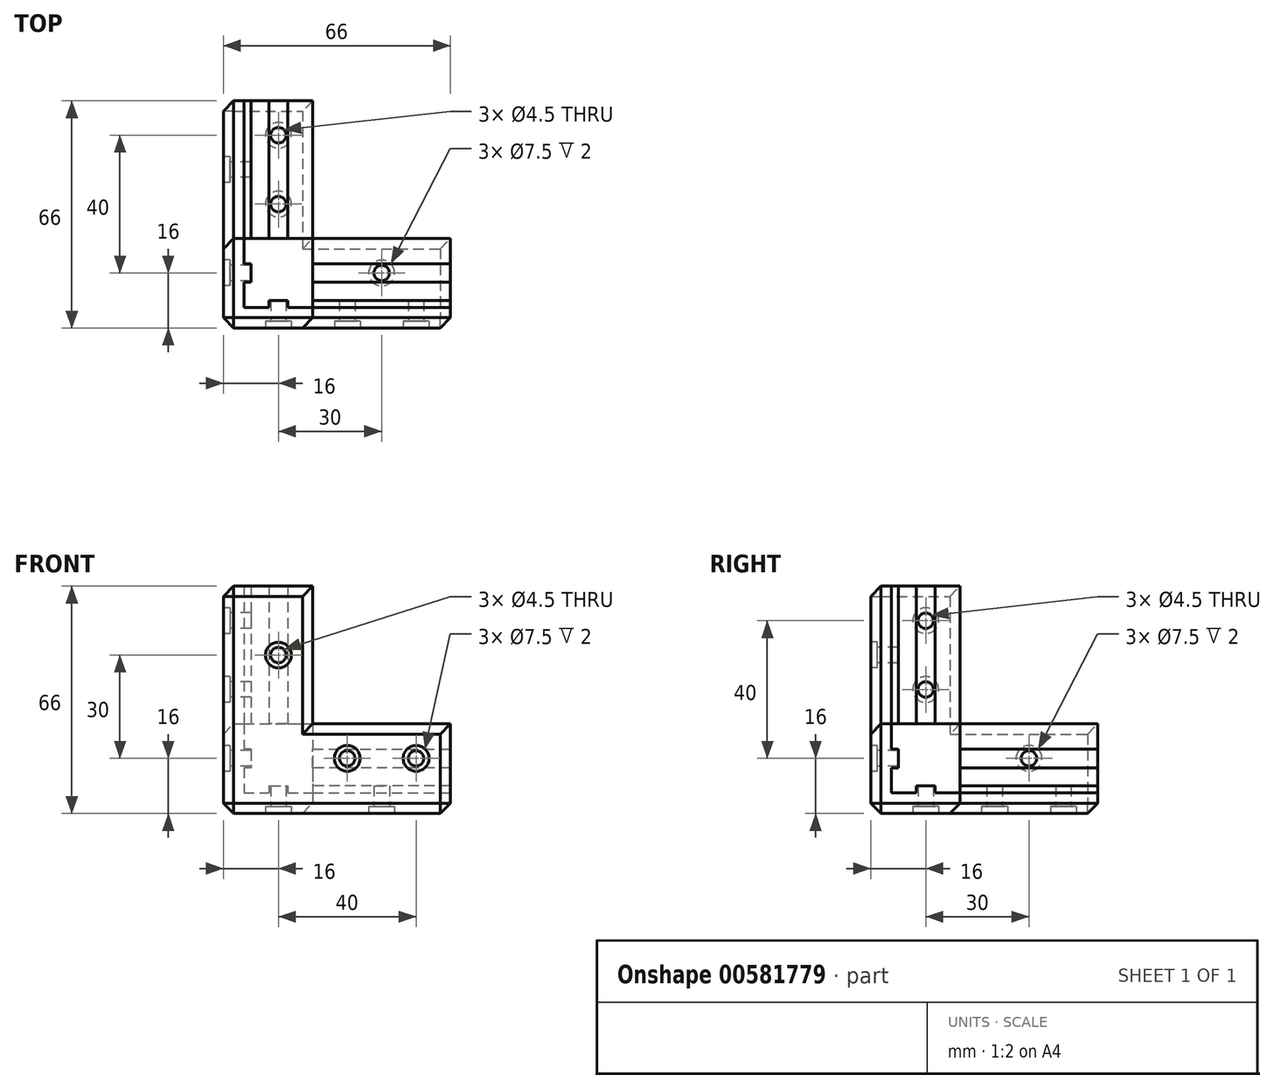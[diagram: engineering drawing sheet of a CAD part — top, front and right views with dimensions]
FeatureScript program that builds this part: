
annotation { "Feature Type Name" : "Feature", "Feature Type Description" : "" }
export const myFeature = defineFeature(function(context is Context, id is Id, definition is map)
    precondition{}
    {
        {
            var Q0;
            Q0=qCreatedBy(makeId("Top.planeOp"),FACE);
            var sketch = newSketch(context, id + "F0", { "sketchPlane" : qUnion([Q0])});
            skLineSegment(sketch, "E0", {"start": v(0, 0) * mm, "end": v(0, 66) * mm});
            skLineSegment(sketch, "E1", {"start": v(0, 66) * mm, "end": v(26, 66) * mm});
            skLineSegment(sketch, "E2", {"start": v(26, 66) * mm, "end": v(26, 26) * mm});
            skLineSegment(sketch, "E3", {"start": v(26, 26) * mm, "end": v(66, 26) * mm});
            skLineSegment(sketch, "E4", {"start": v(66, 26) * mm, "end": v(66, 0) * mm});
            skLineSegment(sketch, "E5", {"start": v(66, 0) * mm, "end": v(0, 0) * mm});
            skLineSegment(sketch, "E6", {"start": v(66, 6) * mm, "end": v(6, 6) * mm, "construction": true});
            skLineSegment(sketch, "E7", {"start": v(6, 6) * mm, "end": v(6, 66) * mm, "construction": true});
            skSolve(sketch);
        }
        {
            var Q0;
            Q0=qSketchRegion(id+"F0",true);
            extrude(context, id + "F1", {"entities" : qUnion([Q0]), "depth" : 6 * mm});
        }
        {
            var Q0;
            Q0=makeQuery(id+"F1.opExtrude","CAP_FACE",FACE,{"disambiguationData":[OSD([sQuery(id+"F0.wireOp",EDGE,"E0"),sQuery(id+"F0.wireOp",EDGE,"E1"),sQuery(id+"F0.wireOp",EDGE,"E2"),sQuery(id+"F0.wireOp",EDGE,"E3"),sQuery(id+"F0.wireOp",EDGE,"E4"),sQuery(id+"F0.wireOp",EDGE,"E5")])],"isStart":false});
            var sketch = newSketch(context, id + "F2", { "sketchPlane" : qUnion([Q0])});
            skLineSegment(sketch, "E8", {"start": v(0, 66) * mm, "end": v(6, 66) * mm});
            skLineSegment(sketch, "E9", {"start": v(6, 66) * mm, "end": v(6, 6) * mm});
            skLineSegment(sketch, "E10", {"start": v(6, 6) * mm, "end": v(66, 6) * mm});
            skLineSegment(sketch, "E11", {"start": v(66, 6) * mm, "end": v(66, 0) * mm});
            skLineSegment(sketch, "E12", {"start": v(66, 0) * mm, "end": v(0, 0) * mm});
            skLineSegment(sketch, "E13", {"start": v(0, 0) * mm, "end": v(0, 66) * mm});
            skSolve(sketch);
        }
        {
            var Q0;
            Q0=makeQuery(id+"F2.imprint","IMPRINT",FACE,{"disambiguationData":[TD([[makeQuery(id+"F2.imprint","IMPRINT",EDGE,{"derivedFrom":sQuery(id+"F2.wireOp",EDGE,"E8")}),-1.0]])]});
            extrude(context, id + "F3", {"entities" : qUnion([Q0]), "operationType" : NewBodyOperationType.ADD, "depth" : 20 * mm});
        }
        {
            var Q0;
            Q0=makeQuery(id+"F3.opExtrude","CAP_FACE",FACE,{"disambiguationData":[OSD([sQuery(id+"F2.wireOp",EDGE,"E8"),sQuery(id+"F2.wireOp",EDGE,"E9"),sQuery(id+"F2.wireOp",EDGE,"E10"),sQuery(id+"F2.wireOp",EDGE,"E11"),sQuery(id+"F2.wireOp",EDGE,"E12"),sQuery(id+"F2.wireOp",EDGE,"E13")])],"isStart":false});
            var sketch = newSketch(context, id + "F4", { "sketchPlane" : qUnion([Q0])});
            skLineSegment(sketch, "E14", {"start": v(6, 26) * mm, "end": v(0, 26) * mm});
            skLineSegment(sketch, "E15", {"start": v(0, 26) * mm, "end": v(0, 0) * mm});
            skLineSegment(sketch, "E16", {"start": v(0, 0) * mm, "end": v(26, 0) * mm});
            skLineSegment(sketch, "E17", {"start": v(26, 0) * mm, "end": v(26, 6) * mm});
            skLineSegment(sketch, "E18", {"start": v(26, 6) * mm, "end": v(6, 6) * mm});
            skLineSegment(sketch, "E19", {"start": v(6, 6) * mm, "end": v(6, 26) * mm});
            skSolve(sketch);
        }
        {
            var Q0;
            Q0=qSketchRegion(id+"F4",true);
            extrude(context, id + "F5", {"entities" : qUnion([Q0]), "operationType" : NewBodyOperationType.ADD, "depth" : 40 * mm});
        }
        {
            var Q0;
            Q0=makeQuery(id+"F1.opExtrude","CAP_FACE",FACE,{"disambiguationData":[OSD([sQuery(id+"F0.wireOp",EDGE,"E0"),sQuery(id+"F0.wireOp",EDGE,"E1"),sQuery(id+"F0.wireOp",EDGE,"E2"),sQuery(id+"F0.wireOp",EDGE,"E3"),sQuery(id+"F0.wireOp",EDGE,"E4"),sQuery(id+"F0.wireOp",EDGE,"E5")])],"isStart":false});
            var sketch = newSketch(context, id + "F6", { "sketchPlane" : qUnion([Q0])});
            skLineSegment(sketch, "E20", {"start": v(66, 16) * mm, "end": v(6, 16) * mm, "construction": true});
            skLineSegment(sketch, "E21", {"start": v(16, 66) * mm, "end": v(16, 6) * mm, "construction": true});
            skLineSegment(sketch, "E22", {"start": v(16, 6) * mm, "end": v(18.71, 6) * mm});
            skLineSegment(sketch, "E23", {"start": v(18.71, 6) * mm, "end": v(18.71, 8) * mm});
            skLineSegment(sketch, "E24", {"start": v(18.71, 8) * mm, "end": v(13.3, 8) * mm});
            skLineSegment(sketch, "E25", {"start": v(13.3, 8) * mm, "end": v(13.3, 6) * mm});
            skLineSegment(sketch, "E26", {"start": v(13.3, 6) * mm, "end": v(16, 6) * mm});
            skLineSegment(sketch, "E27", {"start": v(6, 16) * mm, "end": v(6, 18.7) * mm});
            skLineSegment(sketch, "E28", {"start": v(6, 18.7) * mm, "end": v(8, 18.7) * mm});
            skLineSegment(sketch, "E29", {"start": v(8, 18.7) * mm, "end": v(8, 13.29) * mm});
            skLineSegment(sketch, "E30", {"start": v(8, 13.29) * mm, "end": v(6, 13.29) * mm});
            skLineSegment(sketch, "E31", {"start": v(6, 13.29) * mm, "end": v(6, 16) * mm});
            skSolve(sketch);
        }
        {
            var Q0;
            Q0=qSketchRegion(id+"F6",true);
            extrude(context, id + "F7", {"entities" : qUnion([Q0]), "operationType" : NewBodyOperationType.ADD, "depth" : 60 * mm});
        }
        {
            var Q0;
            Q0=makeQuery(id+"F1.opExtrude","CAP_FACE",FACE,{"disambiguationData":[OSD([sQuery(id+"F0.wireOp",EDGE,"E0"),sQuery(id+"F0.wireOp",EDGE,"E1"),sQuery(id+"F0.wireOp",EDGE,"E2"),sQuery(id+"F0.wireOp",EDGE,"E3"),sQuery(id+"F0.wireOp",EDGE,"E4"),sQuery(id+"F0.wireOp",EDGE,"E5")])],"isStart":false});
            var sketch = newSketch(context, id + "F8", { "sketchPlane" : qUnion([Q0])});
            skLineSegment(sketch, "E32", {"start": v(66, 16) * mm, "end": v(8, 16) * mm, "construction": true});
            skLineSegment(sketch, "E33", {"start": v(66, 16) * mm, "end": v(66, 18.7) * mm});
            skLineSegment(sketch, "E34", {"start": v(66, 18.7) * mm, "end": v(26, 18.7) * mm});
            skLineSegment(sketch, "E35", {"start": v(26, 18.7) * mm, "end": v(26, 13.29) * mm});
            skLineSegment(sketch, "E36", {"start": v(26, 13.29) * mm, "end": v(66, 13.29) * mm});
            skLineSegment(sketch, "E37", {"start": v(66, 13.29) * mm, "end": v(66, 16) * mm});
            skLineSegment(sketch, "E38", {"start": v(16, 66) * mm, "end": v(16, 8) * mm, "construction": true});
            skLineSegment(sketch, "E39", {"start": v(16, 66) * mm, "end": v(13.3, 66) * mm});
            skLineSegment(sketch, "E40", {"start": v(13.3, 66) * mm, "end": v(13.3, 26) * mm});
            skLineSegment(sketch, "E41", {"start": v(13.3, 26) * mm, "end": v(18.7, 26) * mm});
            skLineSegment(sketch, "E42", {"start": v(18.7, 26) * mm, "end": v(18.7, 66) * mm});
            skLineSegment(sketch, "E43", {"start": v(18.7, 66) * mm, "end": v(16, 66) * mm});
            skSolve(sketch);
        }
        {
            var Q0;
            Q0=qSketchRegion(id+"F8",true);
            extrude(context, id + "F9", {"entities" : qUnion([Q0]), "operationType" : NewBodyOperationType.ADD, "depth" : 2 * mm});
        }
        {
            var Q0;
            {var subQ1=sQuery(id+"F2.wireOp",EDGE,"E10");var subQ2=sQuery(id+"F0.wireOp",EDGE,"E4");var subQ3=sQuery(id+"F4.wireOp",EDGE,"E18");Q0=makeQuery(id+"F7.boolean.opBoolean","SPLIT",FACE,{"disambiguationData":[TD([makeQuery(id+"F1.opExtrude","SWEPT_FACE",FACE,{"disambiguationData":[OSD([subQ2])]})])],"derivedFrom":makeQuery(id+"F5.boolean.opBoolean","MERGE",FACE,{"derivedFrom":[makeQuery(id+"F3.opExtrude","SWEPT_FACE",FACE,{"disambiguationData":[OSD([subQ1])]}),makeQuery(id+"F5.opExtrude","SWEPT_FACE",FACE,{"disambiguationData":[OSD([subQ3])]})]})});}
            var sketch = newSketch(context, id + "F10", { "sketchPlane" : qUnion([Q0])});
            skLineSegment(sketch, "E44", {"start": v(-66, 16) * mm, "end": v(-26, 16) * mm, "construction": true});
            skLineSegment(sketch, "E45", {"start": v(-66, 16) * mm, "end": v(-66, 13.3) * mm});
            skLineSegment(sketch, "E46", {"start": v(-66, 13.3) * mm, "end": v(-26, 13.3) * mm});
            skLineSegment(sketch, "E47", {"start": v(-26, 13.3) * mm, "end": v(-26, 16) * mm});
            skLineSegment(sketch, "E48", {"start": v(-26, 18.71) * mm, "end": v(-66, 18.71) * mm});
            skLineSegment(sketch, "E49", {"start": v(-66, 18.71) * mm, "end": v(-66, 16) * mm});
            skLineSegment(sketch, "E50", {"start": v(-26, 18.71) * mm, "end": v(-26, 16) * mm});
            skSolve(sketch);
        }
        {
            var Q0;
            Q0=qSketchRegion(id+"F10",true);
            extrude(context, id + "F11", {"entities" : qUnion([Q0]), "operationType" : NewBodyOperationType.ADD, "depth" : 2 * mm});
        }
        {
            var Q0;
            {var subQ0=sQuery(id+"F2.wireOp",EDGE,"E9");var subQ3=sQuery(id+"F0.wireOp",EDGE,"E1");var subQ5=sQuery(id+"F4.wireOp",EDGE,"E19");Q0=makeQuery(id+"F7.boolean.opBoolean","SPLIT",FACE,{"disambiguationData":[TD([makeQuery(id+"F1.opExtrude","SWEPT_FACE",FACE,{"disambiguationData":[OSD([subQ3])]})])],"derivedFrom":makeQuery(id+"F5.boolean.opBoolean","MERGE",FACE,{"derivedFrom":[makeQuery(id+"F3.opExtrude","SWEPT_FACE",FACE,{"disambiguationData":[OSD([subQ0])]}),makeQuery(id+"F5.opExtrude","SWEPT_FACE",FACE,{"disambiguationData":[OSD([subQ5])]})]})});}
            var sketch = newSketch(context, id + "F12", { "sketchPlane" : qUnion([Q0])});
            skLineSegment(sketch, "E51", {"start": v(66, 16) * mm, "end": v(26, 16) * mm, "construction": true});
            skLineSegment(sketch, "E52", {"start": v(66, 16) * mm, "end": v(66, 18.71) * mm});
            skLineSegment(sketch, "E53", {"start": v(66, 18.71) * mm, "end": v(26, 18.7) * mm});
            skLineSegment(sketch, "E54", {"start": v(26, 18.7) * mm, "end": v(26, 13.29) * mm});
            skLineSegment(sketch, "E55", {"start": v(26, 13.29) * mm, "end": v(66, 13.29) * mm});
            skLineSegment(sketch, "E56", {"start": v(66, 16) * mm, "end": v(66, 13.29) * mm});
            skSolve(sketch);
        }
        {
            var Q0;
            Q0=qSketchRegion(id+"F12",true);
            extrude(context, id + "F13", {"entities" : qUnion([Q0]), "operationType" : NewBodyOperationType.ADD, "depth" : 2 * mm});
        }
        {
            var Q0;
            Q0=makeQuery(id+"F5.boolean.opBoolean","MERGE",FACE,{"derivedFrom":[makeQuery(id+"F3.boolean.opBoolean","MERGE",FACE,{"derivedFrom":[makeQuery(id+"F1.opExtrude","SWEPT_FACE",FACE,{"disambiguationData":[OSD([sQuery(id+"F0.wireOp",EDGE,"E5")])]}),makeQuery(id+"F3.opExtrude","SWEPT_FACE",FACE,{"disambiguationData":[OSD([sQuery(id+"F2.wireOp",EDGE,"E12")])]})]}),makeQuery(id+"F5.opExtrude","SWEPT_FACE",FACE,{"disambiguationData":[OSD([sQuery(id+"F4.wireOp",EDGE,"E16")])]})]});
            var sketch = newSketch(context, id + "F14", { "sketchPlane" : qUnion([Q0])});
            skLineSegment(sketch, "E57", {"start": v(6, 66) * mm, "end": v(6, 6) * mm, "construction": true});
            skLineSegment(sketch, "E58", {"start": v(6, 6) * mm, "end": v(66, 6) * mm, "construction": true});
            skCircle(sketch, "E59", {"center": v(56, 16) * mm, "radius": 2.25 * mm});
            skCircle(sketch, "E60", {"center": v(36, 16) * mm, "radius": 2.25 * mm});
            skCircle(sketch, "E61", {"center": v(16, 46) * mm, "radius": 2.25 * mm});
            skLineSegment(sketch, "E62", {"start": v(26, 26) * mm, "end": v(6, 26) * mm, "construction": true});
            skLineSegment(sketch, "E63", {"start": v(26, 26) * mm, "end": v(26, 6) * mm, "construction": true});
            skSolve(sketch);
        }
        {
            var Q0;
            Q0=makeQuery(id+"F14.imprint","IMPRINT",FACE,{"disambiguationData":[TD([[makeQuery(id+"F14.imprint","IMPRINT",EDGE,{"derivedFrom":sQuery(id+"F14.wireOp",EDGE,"E59")}),1.0]])]});
            var Q1;
            Q1=makeQuery(id+"F14.imprint","IMPRINT",FACE,{"disambiguationData":[TD([[makeQuery(id+"F14.imprint","IMPRINT",EDGE,{"derivedFrom":sQuery(id+"F14.wireOp",EDGE,"E61")}),1.0]])]});
            var Q2;
            Q2=makeQuery(id+"F14.imprint","IMPRINT",FACE,{"disambiguationData":[TD([[makeQuery(id+"F14.imprint","IMPRINT",EDGE,{"derivedFrom":sQuery(id+"F14.wireOp",EDGE,"E60")}),1.0]])]});
            extrude(context, id + "F15", {"entities" : qUnion([Q0, Q1, Q2]), "operationType" : NewBodyOperationType.REMOVE, "endBound" : BoundingType.UP_TO_NEXT, "oppositeDirection" : true, "depth" : 25 * mm});
        }
        {
            var Q0;
            Q0=makeQuery(id+"F5.boolean.opBoolean","MERGE",FACE,{"derivedFrom":[makeQuery(id+"F3.boolean.opBoolean","MERGE",FACE,{"derivedFrom":[makeQuery(id+"F1.opExtrude","SWEPT_FACE",FACE,{"disambiguationData":[OSD([sQuery(id+"F0.wireOp",EDGE,"E0")])]}),makeQuery(id+"F3.opExtrude","SWEPT_FACE",FACE,{"disambiguationData":[OSD([sQuery(id+"F2.wireOp",EDGE,"E13")])]})]}),makeQuery(id+"F5.opExtrude","SWEPT_FACE",FACE,{"disambiguationData":[OSD([sQuery(id+"F4.wireOp",EDGE,"E15")])]})]});
            var sketch = newSketch(context, id + "F16", { "sketchPlane" : qUnion([Q0])});
            skLineSegment(sketch, "E64", {"start": v(-6, 66) * mm, "end": v(-6, 6) * mm, "construction": true});
            skLineSegment(sketch, "E65", {"start": v(-6, 6) * mm, "end": v(-66, 6) * mm, "construction": true});
            skCircle(sketch, "E66", {"center": v(-16, 56) * mm, "radius": 2.25 * mm});
            skCircle(sketch, "E67", {"center": v(-46, 16) * mm, "radius": 2.25 * mm});
            skCircle(sketch, "E68", {"center": v(-16, 36) * mm, "radius": 2.25 * mm});
            skSolve(sketch);
        }
        {
            var Q0;
            Q0=qSketchRegion(id+"F16",true);
            extrude(context, id + "F17", {"entities" : qUnion([Q0]), "operationType" : NewBodyOperationType.REMOVE, "endBound" : BoundingType.UP_TO_NEXT, "oppositeDirection" : true, "depth" : 25 * mm});
        }
        {
            var Q0;
            Q0=makeQuery(id+"F1.opExtrude","CAP_FACE",FACE,{"disambiguationData":[OSD([sQuery(id+"F0.wireOp",EDGE,"E0"),sQuery(id+"F0.wireOp",EDGE,"E1"),sQuery(id+"F0.wireOp",EDGE,"E2"),sQuery(id+"F0.wireOp",EDGE,"E3"),sQuery(id+"F0.wireOp",EDGE,"E4"),sQuery(id+"F0.wireOp",EDGE,"E5")])],"isStart":true});
            var sketch = newSketch(context, id + "F18", { "sketchPlane" : qUnion([Q0])});
            skLineSegment(sketch, "E69", {"start": v(66, -6) * mm, "end": v(6, -6) * mm, "construction": true});
            skLineSegment(sketch, "E70", {"start": v(6, -6) * mm, "end": v(6, -66) * mm, "construction": true});
            skCircle(sketch, "E71", {"center": v(46, -16) * mm, "radius": 2.25 * mm});
            skCircle(sketch, "E72", {"center": v(16, -56) * mm, "radius": 2.25 * mm});
            skCircle(sketch, "E73", {"center": v(16, -36) * mm, "radius": 2.25 * mm});
            skSolve(sketch);
        }
        {
            var Q0;
            Q0=qSketchRegion(id+"F18",true);
            extrude(context, id + "F19", {"entities" : qUnion([Q0]), "operationType" : NewBodyOperationType.REMOVE, "endBound" : BoundingType.UP_TO_NEXT, "oppositeDirection" : true, "depth" : 25 * mm});
        }
        {
            var Q0;
            Q0=makeQuery(id+"F5.boolean.opBoolean","MERGE",FACE,{"derivedFrom":[makeQuery(id+"F3.boolean.opBoolean","MERGE",FACE,{"derivedFrom":[makeQuery(id+"F1.opExtrude","SWEPT_FACE",FACE,{"disambiguationData":[OSD([sQuery(id+"F0.wireOp",EDGE,"E5")])]}),makeQuery(id+"F3.opExtrude","SWEPT_FACE",FACE,{"disambiguationData":[OSD([sQuery(id+"F2.wireOp",EDGE,"E12")])]})]}),makeQuery(id+"F5.opExtrude","SWEPT_FACE",FACE,{"disambiguationData":[OSD([sQuery(id+"F4.wireOp",EDGE,"E16")])]})]});
            var sketch = newSketch(context, id + "F20", { "sketchPlane" : qUnion([Q0])});
            skCircle(sketch, "E74", {"center": v(16, 46) * mm, "radius": 3.75 * mm});
            skCircle(sketch, "E75", {"center": v(36, 16) * mm, "radius": 3.75 * mm});
            skCircle(sketch, "E76", {"center": v(56, 16) * mm, "radius": 3.75 * mm});
            skSolve(sketch);
        }
        {
            var Q0;
            Q0=qSketchRegion(id+"F20",true);
            extrude(context, id + "F21", {"entities" : qUnion([Q0]), "operationType" : NewBodyOperationType.REMOVE, "oppositeDirection" : true, "depth" : 2 * mm});
        }
        {
            var Q0;
            Q0=makeQuery(id+"F5.boolean.opBoolean","MERGE",FACE,{"derivedFrom":[makeQuery(id+"F3.boolean.opBoolean","MERGE",FACE,{"derivedFrom":[makeQuery(id+"F1.opExtrude","SWEPT_FACE",FACE,{"disambiguationData":[OSD([sQuery(id+"F0.wireOp",EDGE,"E0")])]}),makeQuery(id+"F3.opExtrude","SWEPT_FACE",FACE,{"disambiguationData":[OSD([sQuery(id+"F2.wireOp",EDGE,"E13")])]})]}),makeQuery(id+"F5.opExtrude","SWEPT_FACE",FACE,{"disambiguationData":[OSD([sQuery(id+"F4.wireOp",EDGE,"E15")])]})]});
            var sketch = newSketch(context, id + "F22", { "sketchPlane" : qUnion([Q0])});
            skCircle(sketch, "E77", {"center": v(-16, 56) * mm, "radius": 3.75 * mm});
            skCircle(sketch, "E78", {"center": v(-46, 16) * mm, "radius": 3.75 * mm});
            skCircle(sketch, "E79", {"center": v(-16, 36) * mm, "radius": 3.75 * mm});
            skSolve(sketch);
        }
        {
            var Q0;
            Q0=qSketchRegion(id+"F22",true);
            extrude(context, id + "F23", {"entities" : qUnion([Q0]), "operationType" : NewBodyOperationType.REMOVE, "oppositeDirection" : true, "depth" : 2 * mm});
        }
        {
            var Q0;
            Q0=makeQuery(id+"F1.opExtrude","CAP_FACE",FACE,{"disambiguationData":[OSD([sQuery(id+"F0.wireOp",EDGE,"E0"),sQuery(id+"F0.wireOp",EDGE,"E1"),sQuery(id+"F0.wireOp",EDGE,"E2"),sQuery(id+"F0.wireOp",EDGE,"E3"),sQuery(id+"F0.wireOp",EDGE,"E4"),sQuery(id+"F0.wireOp",EDGE,"E5")])],"isStart":true});
            var sketch = newSketch(context, id + "F24", { "sketchPlane" : qUnion([Q0])});
            skCircle(sketch, "E80", {"center": v(16, -56) * mm, "radius": 3.75 * mm});
            skCircle(sketch, "E81", {"center": v(46, -16) * mm, "radius": 3.75 * mm});
            skCircle(sketch, "E82", {"center": v(16, -36) * mm, "radius": 3.75 * mm});
            skSolve(sketch);
        }
        {
            var Q0;
            Q0=qSketchRegion(id+"F24",true);
            extrude(context, id + "F25", {"entities" : qUnion([Q0]), "operationType" : NewBodyOperationType.REMOVE, "oppositeDirection" : true, "depth" : 2 * mm});
        }
        {
            var Q0;
            Q0=makeQuery(id+"F1.opExtrude","CAP_EDGE",EDGE,{"disambiguationData":[OSD([sQuery(id+"F0.wireOp",EDGE,"E5")])],"isStart":true});
            var Q1;
            Q1=makeQuery(id+"F1.opExtrude","CAP_EDGE",EDGE,{"disambiguationData":[OSD([sQuery(id+"F0.wireOp",EDGE,"E0")])],"isStart":true});
            var Q2;
            Q2=makeQuery(id+"F5.boolean.opBoolean","MERGE",EDGE,{"derivedFrom":[makeQuery(id+"F3.boolean.opBoolean","MERGE",EDGE,{"derivedFrom":[makeQuery(id+"F1.opExtrude","SWEPT_EDGE",EDGE,{"disambiguationData":[OSD([sQuery(id+"F0.wireOp",EDGE,"E0"),sQuery(id+"F0.wireOp",EDGE,"E5")])]}),makeQuery(id+"F3.opExtrude","SWEPT_EDGE",EDGE,{"disambiguationData":[OSD([sQuery(id+"F2.wireOp",EDGE,"E12"),sQuery(id+"F2.wireOp",EDGE,"E13")])]})]}),makeQuery(id+"F5.opExtrude","SWEPT_EDGE",EDGE,{"disambiguationData":[OSD([sQuery(id+"F4.wireOp",EDGE,"E15"),sQuery(id+"F4.wireOp",EDGE,"E16")])]})]});
            var Q3;
            Q3=makeQuery(id+"F5.opExtrude","SWEPT_EDGE",EDGE,{"disambiguationData":[OSD([sQuery(id+"F2.wireOp",EDGE,"E13"),sQuery(id+"F4.wireOp",EDGE,"E14"),sQuery(id+"F4.wireOp",EDGE,"E15")])]});
            var Q4;
            Q4=makeQuery(id+"F3.opExtrude","CAP_EDGE",EDGE,{"disambiguationData":[OSD([sQuery(id+"F2.wireOp",EDGE,"E13")])],"isStart":false});
            var Q5;
            Q5=makeQuery(id+"F5.opExtrude","SWEPT_EDGE",EDGE,{"disambiguationData":[OSD([sQuery(id+"F2.wireOp",EDGE,"E12"),sQuery(id+"F4.wireOp",EDGE,"E16"),sQuery(id+"F4.wireOp",EDGE,"E17")])]});
            var Q6;
            Q6=makeQuery(id+"F3.opExtrude","CAP_EDGE",EDGE,{"disambiguationData":[OSD([sQuery(id+"F2.wireOp",EDGE,"E12")])],"isStart":false});
            var Q7;
            Q7=makeQuery(id+"F5.opExtrude","CAP_EDGE",EDGE,{"disambiguationData":[OSD([sQuery(id+"F4.wireOp",EDGE,"E15")])],"isStart":false});
            var Q8;
            Q8=makeQuery(id+"F5.opExtrude","CAP_EDGE",EDGE,{"disambiguationData":[OSD([sQuery(id+"F4.wireOp",EDGE,"E16")])],"isStart":false});
            var Q9;
            Q9=makeQuery(id+"F3.boolean.opBoolean","MERGE",EDGE,{"derivedFrom":[makeQuery(id+"F1.opExtrude","SWEPT_EDGE",EDGE,{"disambiguationData":[OSD([sQuery(id+"F0.wireOp",EDGE,"E0"),sQuery(id+"F0.wireOp",EDGE,"E1")])]}),makeQuery(id+"F3.opExtrude","SWEPT_EDGE",EDGE,{"disambiguationData":[OSD([sQuery(id+"F2.wireOp",EDGE,"E8"),sQuery(id+"F2.wireOp",EDGE,"E13")])]})]});
            var Q10;
            Q10=makeQuery(id+"F1.opExtrude","CAP_EDGE",EDGE,{"disambiguationData":[OSD([sQuery(id+"F0.wireOp",EDGE,"E1")])],"isStart":true});
            var Q11;
            Q11=makeQuery(id+"F3.boolean.opBoolean","MERGE",EDGE,{"derivedFrom":[makeQuery(id+"F1.opExtrude","SWEPT_EDGE",EDGE,{"disambiguationData":[OSD([sQuery(id+"F0.wireOp",EDGE,"E4"),sQuery(id+"F0.wireOp",EDGE,"E5")])]}),makeQuery(id+"F3.opExtrude","SWEPT_EDGE",EDGE,{"disambiguationData":[OSD([sQuery(id+"F2.wireOp",EDGE,"E11"),sQuery(id+"F2.wireOp",EDGE,"E12")])]})]});
            var Q12;
            Q12=makeQuery(id+"F1.opExtrude","CAP_EDGE",EDGE,{"disambiguationData":[OSD([sQuery(id+"F0.wireOp",EDGE,"E4")])],"isStart":true});
            var Q13;
            Q13=makeQuery(id+"F1.opExtrude","CAP_EDGE",EDGE,{"disambiguationData":[OSD([sQuery(id+"F0.wireOp",EDGE,"E3")])],"isStart":true});
            var Q14;
            Q14=makeQuery(id+"F1.opExtrude","CAP_EDGE",EDGE,{"disambiguationData":[OSD([sQuery(id+"F0.wireOp",EDGE,"E2")])],"isStart":true});
            chamfer(context, id + "F26", {"entities" : qUnion([Q0, Q1, Q2, Q3, Q4, Q5, Q6, Q7, Q8, Q9, Q10, Q11, Q12, Q13, Q14]), "width" : 3 * mm, "tangentPropagation" : true});
        }
        {
            var Q0;
            Q0=makeQuery(id+"F1.opExtrude","CAP_FACE",FACE,{"disambiguationData":[OSD([sQuery(id+"F0.wireOp",EDGE,"E0"),sQuery(id+"F0.wireOp",EDGE,"E1"),sQuery(id+"F0.wireOp",EDGE,"E2"),sQuery(id+"F0.wireOp",EDGE,"E3"),sQuery(id+"F0.wireOp",EDGE,"E4"),sQuery(id+"F0.wireOp",EDGE,"E5")])],"isStart":false});
            var sketch = newSketch(context, id + "F27", { "sketchPlane" : qUnion([Q0])});
            skLineSegment(sketch, "E83.bottom", {"start": v(6, 6) * mm, "end": v(26, 6) * mm});
            skLineSegment(sketch, "E83.top", {"start": v(6, 26) * mm, "end": v(26, 26) * mm});
            skLineSegment(sketch, "E83.left", {"start": v(6, 6) * mm, "end": v(6, 26) * mm});
            skLineSegment(sketch, "E83.right", {"start": v(26, 6) * mm, "end": v(26, 26) * mm});
            skSolve(sketch);
        }
        {
            var Q0;
            Q0=qSketchRegion(id+"F27",true);
            extrude(context, id + "F28", {"entities" : qUnion([Q0]), "operationType" : NewBodyOperationType.ADD, "depth" : 20 * mm});
        }
    });
